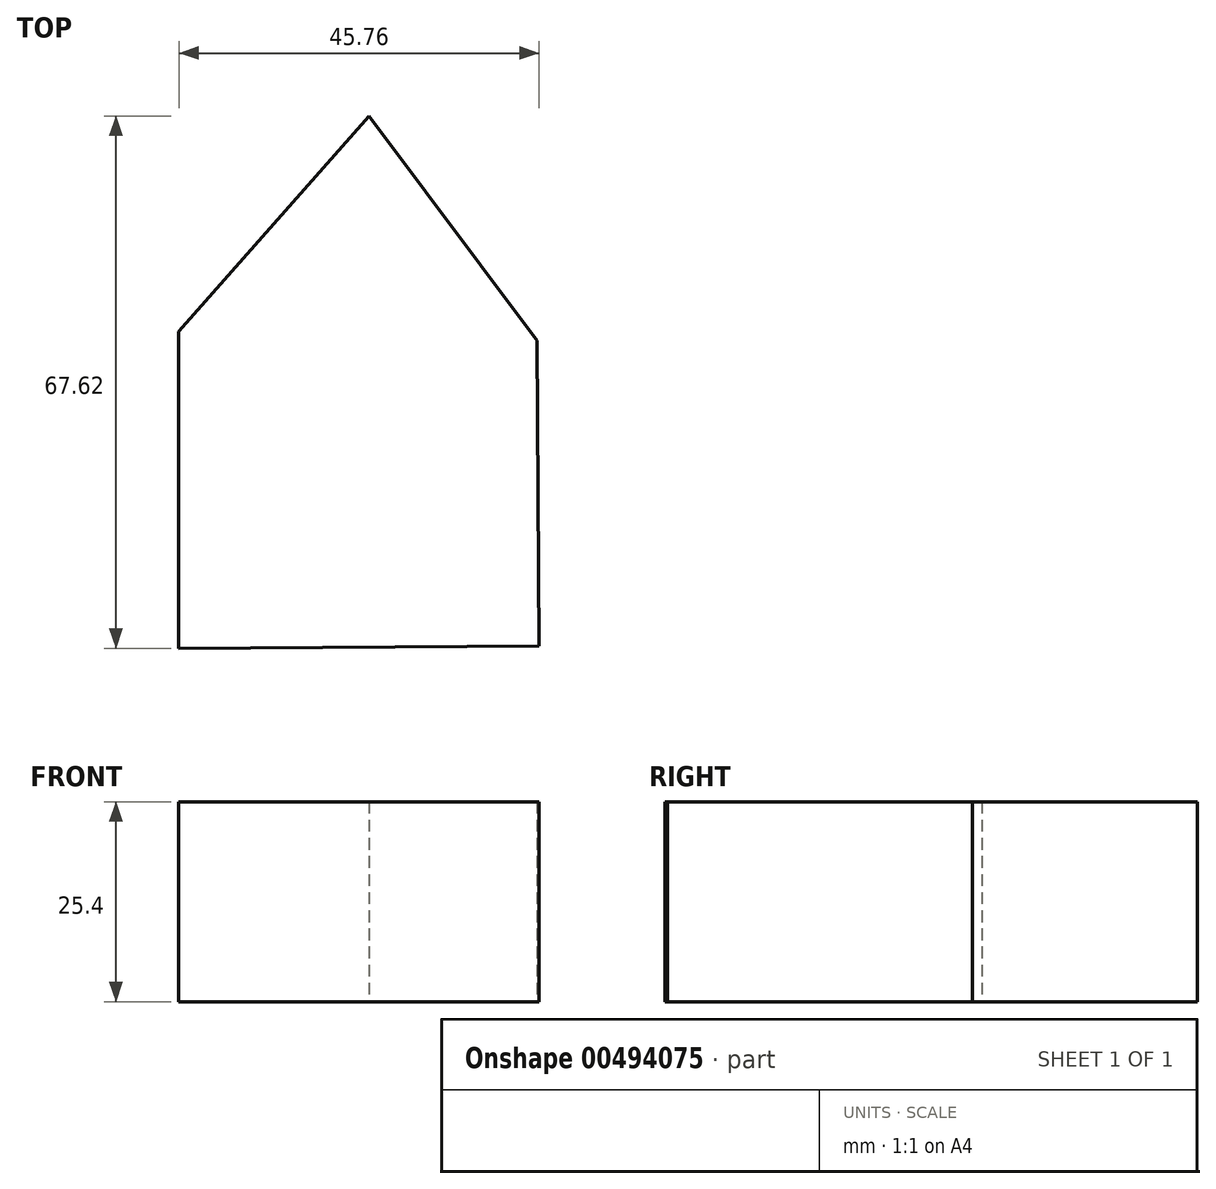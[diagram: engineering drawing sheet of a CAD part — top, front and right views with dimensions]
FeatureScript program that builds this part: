
annotation { "Feature Type Name" : "Feature", "Feature Type Description" : "" }
export const myFeature = defineFeature(function(context is Context, id is Id, definition is map)
    precondition{}
    {
        {
            var Q0;
            Q0=qCreatedBy(makeId("Top.planeOp"),FACE);
            var sketch = newSketch(context, id + "F0", { "sketchPlane" : qUnion([Q0])});
            skLineSegment(sketch, "E0", {"start": v(0, 19.1) * mm, "end": v(-24.2, -8.3) * mm});
            skLineSegment(sketch, "E1", {"start": v(-24.2, -8.3) * mm, "end": v(-24.2, -48.53) * mm});
            skLineSegment(sketch, "E2", {"start": v(-24.2, -48.53) * mm, "end": v(21.57, -48.24) * mm});
            skLineSegment(sketch, "E3", {"start": v(21.57, -48.24) * mm, "end": v(21.32, -9.47) * mm});
            skLineSegment(sketch, "E4", {"start": v(21.32, -9.47) * mm, "end": v(0, 19.1) * mm});
            skSolve(sketch);
        }
        {
            var Q0;
            Q0=makeQuery(id+"F0.imprint","IMPRINT",FACE,{"disambiguationData":[TD([[makeQuery(id+"F0.imprint","IMPRINT",EDGE,{"derivedFrom":sQuery(id+"F0.wireOp",EDGE,"E0")}),1.0]])]});
            extrude(context, id + "F1", {"entities" : qUnion([Q0]), "depth" : 25.4 * mm});
        }
    });
